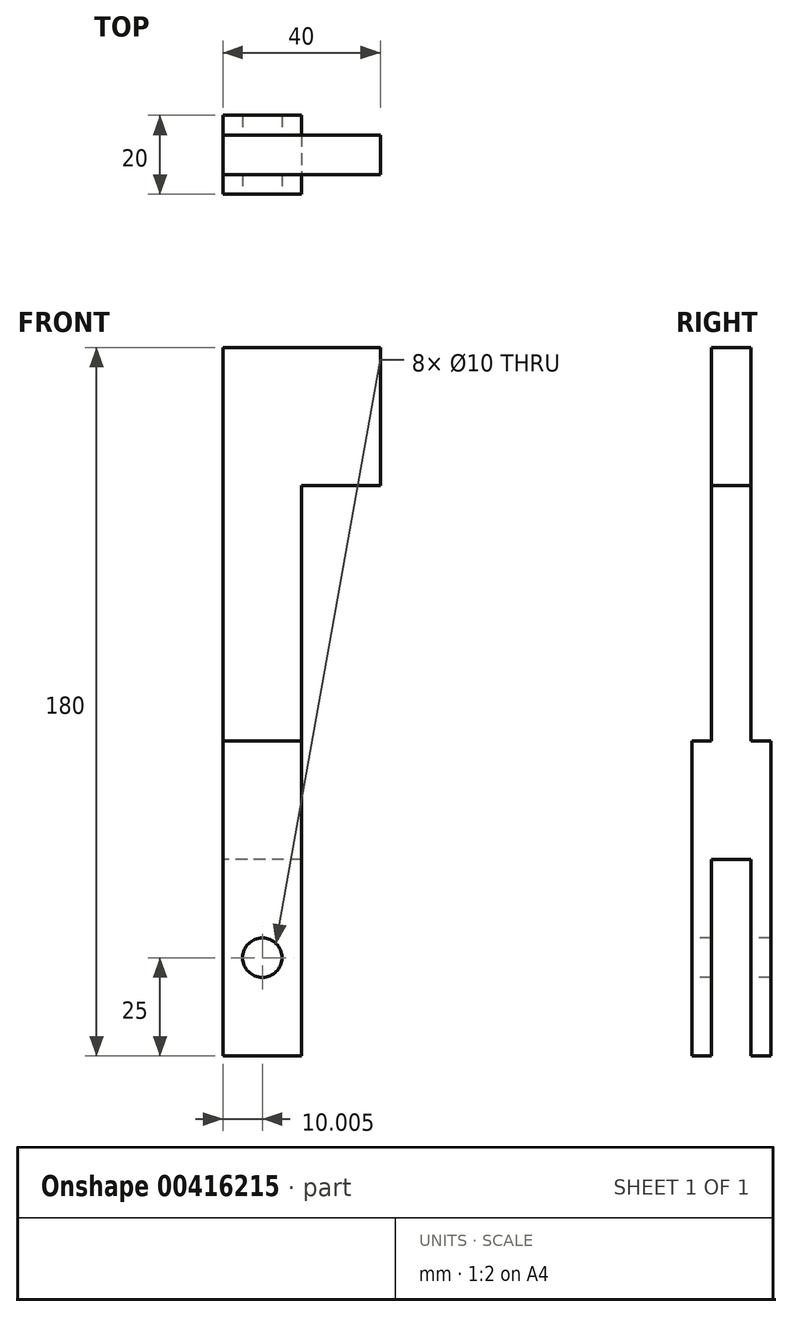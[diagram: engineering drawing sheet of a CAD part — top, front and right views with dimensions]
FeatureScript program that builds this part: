
annotation { "Feature Type Name" : "Feature", "Feature Type Description" : "" }
export const myFeature = defineFeature(function(context is Context, id is Id, definition is map)
    precondition{}
    {
        {
            var Q0;
            Q0=qCreatedBy(makeId("Front.planeOp"),FACE);
            var sketch = newSketch(context, id + "F0", { "sketchPlane" : qUnion([Q0])});
            skLineSegment(sketch, "E0", {"start": v(-19.26, 0) * mm, "end": v(-19.26, 180) * mm});
            skLineSegment(sketch, "E1", {"start": v(-19.26, 180) * mm, "end": v(20.74, 180) * mm});
            skLineSegment(sketch, "E2", {"start": v(20.74, 180) * mm, "end": v(20.74, 145) * mm});
            skLineSegment(sketch, "E3", {"start": v(20.74, 145) * mm, "end": v(0.74, 145) * mm});
            skLineSegment(sketch, "E4", {"start": v(0.74, 145) * mm, "end": v(0.74, 0) * mm});
            skLineSegment(sketch, "E5", {"start": v(0.74, 0) * mm, "end": v(-19.26, 0) * mm});
            skSolve(sketch);
        }
        {
            var Q0;
            Q0 = qSketchRegion(id + "F0", true);
            extrude(context, id + "F1", {"entities" : qUnion([Q0]), "oppositeDirection" : true, "depth" : 20 * mm});
        }
        {
            var Q0;
            Q0=makeQuery(id+"F1.opExtrude","SWEPT_FACE",FACE,{"disambiguationData":[OSD([sQuery(id+"F0.wireOp",EDGE,"E1")])]});
            var sketch = newSketch(context, id + "F2", { "sketchPlane" : qUnion([Q0])});
            skLineSegment(sketch, "E6.bottom", {"start": v(-19.26, 20) * mm, "end": v(20.74, 20) * mm});
            skLineSegment(sketch, "E6.top", {"start": v(-19.26, 15) * mm, "end": v(20.74, 15) * mm});
            skLineSegment(sketch, "E6.left", {"start": v(-19.26, 20) * mm, "end": v(-19.26, 15) * mm});
            skLineSegment(sketch, "E6.right", {"start": v(20.74, 20) * mm, "end": v(20.74, 15) * mm});
            skLineSegment(sketch, "E7.bottom", {"start": v(20.74, 0) * mm, "end": v(-19.26, 0) * mm});
            skLineSegment(sketch, "E7.top", {"start": v(20.74, 5) * mm, "end": v(-19.26, 5) * mm});
            skLineSegment(sketch, "E7.left", {"start": v(20.74, 0) * mm, "end": v(20.74, 5) * mm});
            skLineSegment(sketch, "E7.right", {"start": v(-19.26, 0) * mm, "end": v(-19.26, 5) * mm});
            skSolve(sketch);
        }
        {
            var Q0;
            Q0 = qSketchRegion(id + "F2", true);
            extrude(context, id + "F3", {"entities" : qUnion([Q0]), "operationType" : NewBodyOperationType.REMOVE, "oppositeDirection" : true, "depth" : 100 * mm});
        }
        {
            var Q0;
            Q0=makeQuery(id+"F1.opExtrude","SWEPT_FACE",FACE,{"disambiguationData":[OSD([sQuery(id+"F0.wireOp",EDGE,"E5")])]});
            var sketch = newSketch(context, id + "F4", { "sketchPlane" : qUnion([Q0])});
            skLineSegment(sketch, "E8.bottom", {"start": v(0.74, -15) * mm, "end": v(-19.26, -15) * mm});
            skLineSegment(sketch, "E8.top", {"start": v(0.74, -5) * mm, "end": v(-19.26, -5) * mm});
            skLineSegment(sketch, "E8.left", {"start": v(0.74, -15) * mm, "end": v(0.74, -5) * mm});
            skLineSegment(sketch, "E8.right", {"start": v(-19.26, -15) * mm, "end": v(-19.26, -5) * mm});
            skSolve(sketch);
        }
        {
            var Q0;
            Q0 = qSketchRegion(id + "F4", true);
            extrude(context, id + "F5", {"entities" : qUnion([Q0]), "operationType" : NewBodyOperationType.REMOVE, "oppositeDirection" : true, "depth" : 50 * mm});
        }
        {
            var Q0;
            Q0=makeQuery(id+"F1.opExtrude","CAP_FACE",FACE,{"disambiguationData":[OSD([sQuery(id+"F0.wireOp",EDGE,"E0"),sQuery(id+"F0.wireOp",EDGE,"E1"),sQuery(id+"F0.wireOp",EDGE,"E2"),sQuery(id+"F0.wireOp",EDGE,"E3"),sQuery(id+"F0.wireOp",EDGE,"E4"),sQuery(id+"F0.wireOp",EDGE,"E5")])],"isStart":true});
            var sketch = newSketch(context, id + "F6", { "sketchPlane" : qUnion([Q0])});
            skCircle(sketch, "E9", {"center": v(-9.26, 25) * mm, "radius": 5 * mm});
            skSolve(sketch);
        }
        {
            var Q0;
            Q0 = qSketchRegion(id + "F6", true);
            extrude(context, id + "F7", {"entities" : qUnion([Q0]), "operationType" : NewBodyOperationType.REMOVE, "endBound" : BoundingType.THROUGH_ALL, "oppositeDirection" : true, "depth" : 25 * mm});
        }
    });
